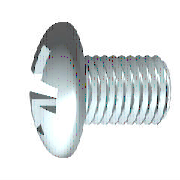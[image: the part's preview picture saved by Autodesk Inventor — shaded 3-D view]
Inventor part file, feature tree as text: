
AUTODESK INVENTOR PART (.ipt)
format: ipt  version: 2016 (Build 200138000, 138)  size: 270,336 bytes
history: native  units: mm (DEFAULTED — no unit token found)
features: extrude x1, other x1, plane x1
ambient origin geometry x7: Origin, YZ Plane, XZ Plane, X Axis, Y Axis, Z Axis, Center Point
bodies: Solid1 (feature_tree), Body (feature_tree)
feature tree (3):
  extrude  "Slot"  Depth=2.5mm
  other  "Cut"
  plane  "Work Plane3"
